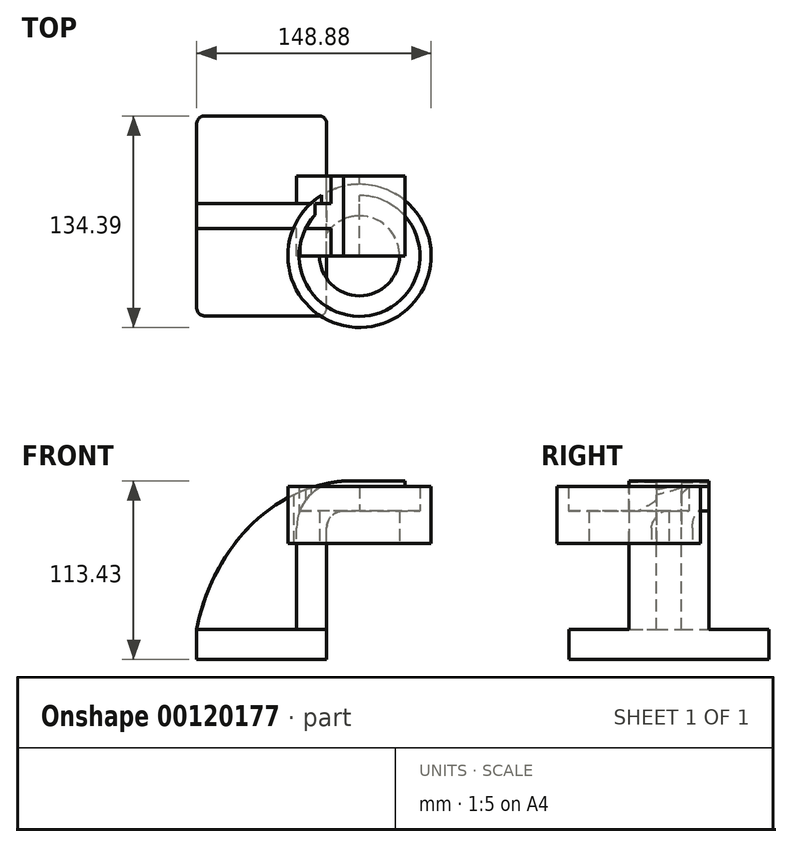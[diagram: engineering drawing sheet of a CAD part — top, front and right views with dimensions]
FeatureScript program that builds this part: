
annotation { "Feature Type Name" : "Feature", "Feature Type Description" : "" }
export const myFeature = defineFeature(function(context is Context, id is Id, definition is map)
    precondition{}
    {
        {
            var Q0;
            Q0=qCreatedBy(makeId("Front.planeOp"),FACE);
            var sketch = newSketch(context, id + "F0", { "sketchPlane" : qUnion([Q0])});
            skLineSegment(sketch, "E0.bottom", {"start": v(41.27, 9.53) * mm, "end": v(-41.28, 9.53) * mm});
            skLineSegment(sketch, "E0.top", {"start": v(41.28, -9.52) * mm, "end": v(-41.27, -9.52) * mm});
            skLineSegment(sketch, "E0.left", {"start": v(41.28, 9.53) * mm, "end": v(41.28, -9.52) * mm});
            skLineSegment(sketch, "E0.right", {"start": v(-41.28, 9.53) * mm, "end": v(-41.27, -9.52) * mm});
            skPoint(sketch, "E0.middle", {"position": v(0, 0) * mm});
            skLineSegment(sketch, "E1.bottom", {"start": v(99.85, 64.27) * mm, "end": v(62.1, 64.27) * mm});
            skLineSegment(sketch, "E1.top", {"start": v(99.85, 100.44) * mm, "end": v(62.1, 100.44) * mm});
            skLineSegment(sketch, "E1.left", {"start": v(99.85, 64.27) * mm, "end": v(99.85, 100.44) * mm});
            skLineSegment(sketch, "E1.right", {"start": v(62.1, 64.27) * mm, "end": v(62.1, 100.44) * mm});
            skPoint(sketch, "E1.middle", {"position": v(80.98, 82.35) * mm});
            skLineSegment(sketch, "E2", {"start": v(41.27, 9.53) * mm, "end": v(41.27, 74.2) * mm});
            skArc(sketch, "E3", {"start": v(41.27, 74.2) * mm, "mid": v(44.4, 81.73) * mm, "end": v(51.92, 84.85) * mm});
            skLineSegment(sketch, "E4", {"start": v(51.92, 84.85) * mm, "end": v(90.87, 84.85) * mm});
            skLineSegment(sketch, "E5.0", {"start": v(22.22, 9.53) * mm, "end": v(22.22, 74.2) * mm});
            skArc(sketch, "E6.0", {"start": v(22.22, 74.2) * mm, "mid": v(30.92, 95.2) * mm, "end": v(51.92, 103.9) * mm});
            skLineSegment(sketch, "E7.0", {"start": v(51.92, 103.9) * mm, "end": v(90.87, 103.9) * mm});
            skFitSpline(sketch, "E8", {"points": [v(-41.28, 9.53) * mm, v(51.92, 103.9) * mm], "startDerivative": vector(24.12, 131.35) * mm, "endDerivative": vector(155.76, 14.2) * mm});
            skLineSegment(sketch, "E9", {"start": v(90.87, 103.9) * mm, "end": v(90.87, 84.85) * mm});
            skSolve(sketch);
        }
        {
            var Q0;
            Q0=makeQuery(id+"F0.imprint","IMPRINT",FACE,{"disambiguationData":[TD([[makeQuery(id+"F0.imprint","IMPRINT",EDGE,{"derivedFrom":sQuery(id+"F0.wireOp",EDGE,"E0.top")}),-1.0]])]});
            extrude(context, id + "F1", {"entities" : qUnion([Q0]), "endBound" : BoundingType.SYMMETRIC, "depth" : 127 * mm});
        }
        {
            var Q0;
            {var subQ9=sQuery(id+"F0.wireOp",EDGE,"E2");Q0=makeQuery(id+"F0.imprint","IMPRINT",FACE,{"disambiguationData":[TD([[makeQuery(id+"F0.imprint","IMPRINT",EDGE,{"derivedFrom":subQ9}),1.0]])]});}
            extrude(context, id + "F2", {"entities" : qUnion([Q0]), "operationType" : NewBodyOperationType.ADD, "endBound" : BoundingType.SYMMETRIC, "depth" : 50.8 * mm});
        }
        {
            var Q0;
            {var subQ3=sQuery(id+"F0.wireOp",EDGE,"E5.0");Q0=makeQuery(id+"F0.imprint","IMPRINT",FACE,{"disambiguationData":[TD([[makeQuery(id+"F0.imprint","IMPRINT",EDGE,{"derivedFrom":subQ3}),1.0]])]});}
            extrude(context, id + "F3", {"entities" : qUnion([Q0]), "operationType" : NewBodyOperationType.ADD, "endBound" : BoundingType.SYMMETRIC, "depth" : 15.88 * mm});
        }
        {
            var Q0;
            {var subQ1=sQuery(id+"F0.wireOp",EDGE,"E1.bottom");Q0=makeQuery(id+"F0.imprint","IMPRINT",FACE,{"disambiguationData":[TD([[makeQuery(id+"F0.imprint","IMPRINT",EDGE,{"derivedFrom":subQ1}),-1.0]])]});}
            var Q1;
            Q1=makeQuery(id+"F2.opExtrude","CAP_EDGE",EDGE,{"disambiguationData":[OSD([sQuery(id+"F0.wireOp",EDGE,"E1.right")])],"isStart":false});
            revolve(context, id + "F4", {"operationType" : NewBodyOperationType.ADD, "entities" : qUnion([Q0]), "axis" : qUnion([Q1]), "revolveType" : RevolveType.FULL});
        }
        {
            var Q0;
            Q0=makeQuery(id+"F1.opExtrude","CAP_EDGE",EDGE,{"disambiguationData":[OSD([sQuery(id+"F0.wireOp",EDGE,"E0.right")])],"isStart":false});
            var Q1;
            Q1=makeQuery(id+"F1.opExtrude","CAP_EDGE",EDGE,{"disambiguationData":[OSD([sQuery(id+"F0.wireOp",EDGE,"E0.left")])],"isStart":false});
            var Q2;
            Q2=makeQuery(id+"F1.opExtrude","CAP_EDGE",EDGE,{"disambiguationData":[OSD([sQuery(id+"F0.wireOp",EDGE,"E0.left")])],"isStart":true});
            var Q3;
            Q3=makeQuery(id+"F1.opExtrude","CAP_EDGE",EDGE,{"disambiguationData":[OSD([sQuery(id+"F0.wireOp",EDGE,"E0.right")])],"isStart":true});
            fillet(context, id + "F5", {"entities" : qUnion([Q0, Q1, Q2, Q3]), "radius" : 5.08 * mm, "tangentPropagation" : true, "allowEdgeOverflow" : false});
        }
    });
